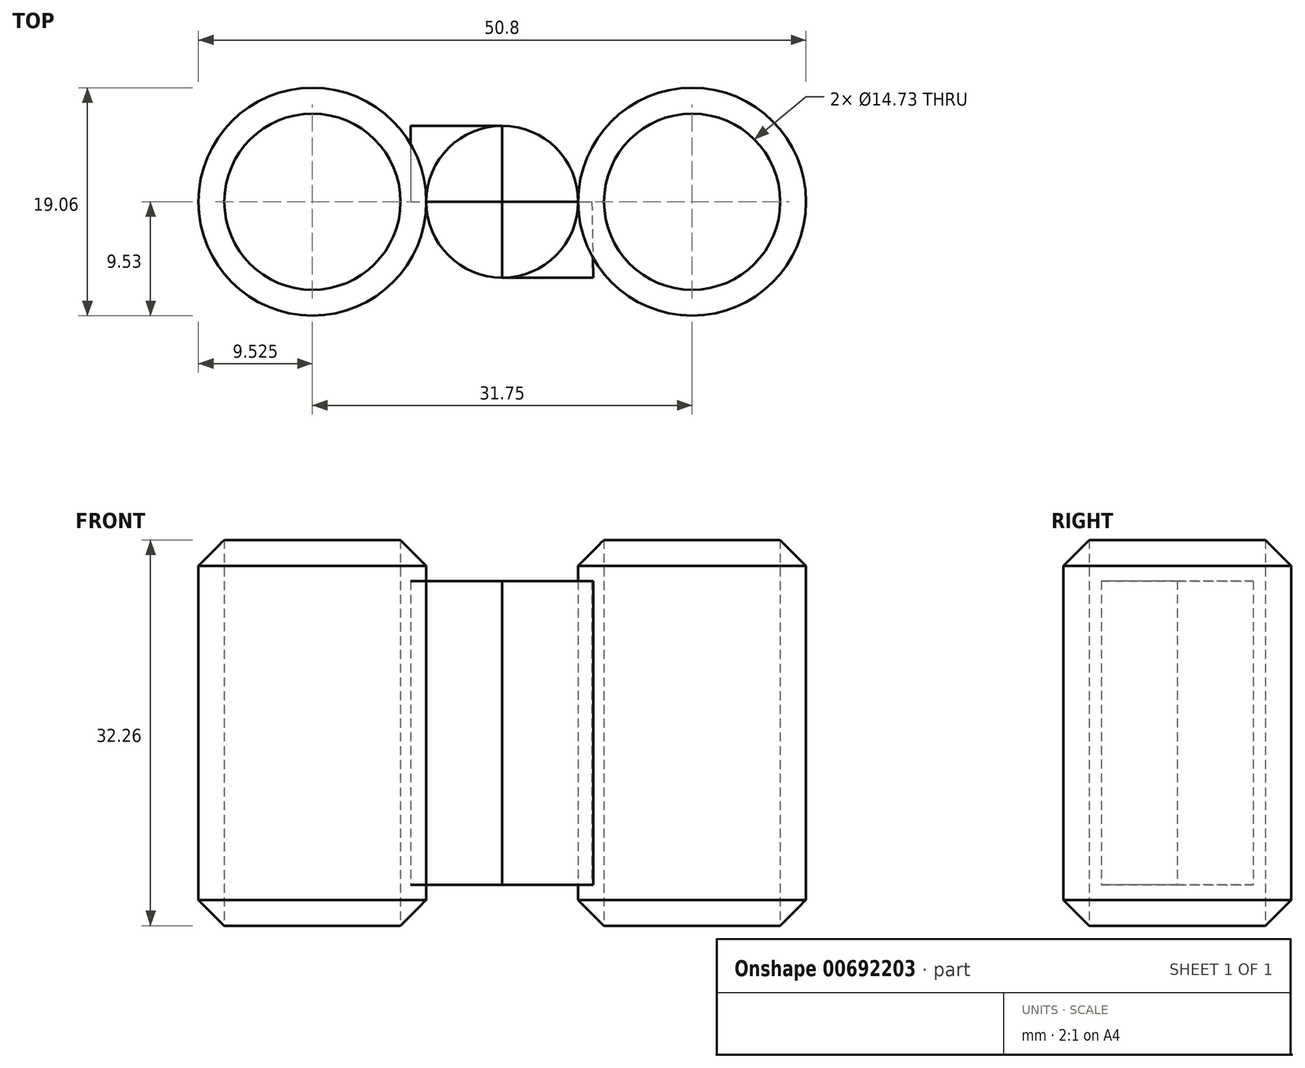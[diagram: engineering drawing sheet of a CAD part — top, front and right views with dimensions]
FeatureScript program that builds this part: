
annotation { "Feature Type Name" : "Feature", "Feature Type Description" : "" }
export const myFeature = defineFeature(function(context is Context, id is Id, definition is map)
    precondition{}
    {
        {
            var Q0;
            Q0=qCreatedBy(makeId("Top.planeOp"),FACE);
            var sketch = newSketch(context, id + "F0", { "sketchPlane" : qUnion([Q0])});
            skCircle(sketch, "E0", {"center": v(-15.88, 0) * mm, "radius": 7.37 * mm});
            skCircle(sketch, "E1.MirrorC", {"center": v(15.88, 0) * mm, "radius": 7.37 * mm});
            skCircle(sketch, "E2", {"center": v(-15.88, 0) * mm, "radius": 9.53 * mm});
            skCircle(sketch, "E3.MirrorC", {"center": v(15.88, 0) * mm, "radius": 9.53 * mm});
            skSolve(sketch);
        }
        {
            var Q0;
            Q0=qSketchRegion(id+"F0",true);
            extrude(context, id + "F1", {"entities" : qUnion([Q0]), "endBound" : BoundingType.SYMMETRIC, "depth" : 38.1 * mm, "offsetDistance" : 25.4 * mm});
        }
        {
            var Q0;
            Q0=qCreatedBy(makeId("Top.planeOp"),FACE);
            var sketch = newSketch(context, id + "F2", { "sketchPlane" : qUnion([Q0])});
            skCircle(sketch, "E4", {"center": v(0, 0) * mm, "radius": 6.35 * mm});
            skSolve(sketch);
        }
        {
            var Q0;
            Q0=qSketchRegion(id+"F2",true);
            extrude(context, id + "F3", {"entities" : qUnion([Q0]), "endBound" : BoundingType.SYMMETRIC, "depth" : 25.4 * mm, "offsetDistance" : 25.4 * mm});
        }
        {
            var Q0;
            Q0=qCreatedBy(makeId("Top.planeOp"),FACE);
            var sketch = newSketch(context, id + "F4", { "sketchPlane" : qUnion([Q0])});
            skLineSegment(sketch, "E5", {"start": v(0, 0) * mm, "end": v(0, 6.35) * mm});
            skLineSegment(sketch, "E6", {"start": v(0, 6.35) * mm, "end": v(-7.65, 6.35) * mm});
            skLineSegment(sketch, "E7", {"start": v(-7.65, 6.35) * mm, "end": v(7.6, 6.35) * mm});
            skPoint(sketch, "E7.endSnap0", {"position": v(-3.82, 6.35) * mm});
            skLineSegment(sketch, "E8", {"start": v(-7.65, 6.35) * mm, "end": v(-7.65, 0) * mm});
            skLineSegment(sketch, "E9", {"start": v(-7.65, 0) * mm, "end": v(7.5, 0) * mm});
            skLineSegment(sketch, "E10", {"start": v(7.5, 0) * mm, "end": v(7.6, 6.35) * mm});
            skLineSegment(sketch, "E11.MirrorCS", {"start": v(-7.65, -6.35) * mm, "end": v(7.6, -6.35) * mm});
            skLineSegment(sketch, "E12.MirrorCS", {"start": v(-7.65, -6.35) * mm, "end": v(-7.65, 0) * mm});
            skLineSegment(sketch, "E13.MirrorCS", {"start": v(7.5, 0) * mm, "end": v(7.6, -6.35) * mm});
            skLineSegment(sketch, "E14.MirrorCS", {"start": v(0, 0) * mm, "end": v(0, -6.35) * mm});
            skSolve(sketch);
        }
        {
            var Q0;
            {var subQ0=sQuery(id+"F4.wireOp",EDGE,"E5");Q0=makeQuery(id+"F4.imprint","IMPRINT",FACE,{"disambiguationData":[TD([[makeQuery(id+"F4.imprint","IMPRINT",EDGE,{"derivedFrom":subQ0}),1.0]])]});}
            var Q1;
            {var subQ2=sQuery(id+"F4.wireOp",EDGE,"E13.MirrorCS");Q1=makeQuery(id+"F4.imprint","IMPRINT",FACE,{"disambiguationData":[TD([[makeQuery(id+"F4.imprint","IMPRINT",EDGE,{"derivedFrom":subQ2}),-1.0]])]});}
            extrude(context, id + "F5", {"entities" : qUnion([Q0, Q1]), "endBound" : BoundingType.SYMMETRIC, "depth" : 25.4 * mm, "offsetDistance" : 25.4 * mm});
        }
        {
            var Q0;
            Q0=makeQuery(id+"F1.opExtrude","CAP_EDGE",EDGE,{"disambiguationData":[OSD([sQuery(id+"F0.wireOp",EDGE,"E3.MirrorC")])],"isStart":false});
            var Q1;
            Q1=makeQuery(id+"F1.opExtrude","CAP_EDGE",EDGE,{"disambiguationData":[OSD([sQuery(id+"F0.wireOp",EDGE,"E2")])],"isStart":false});
            var Q2;
            Q2=makeQuery(id+"F1.opExtrude","CAP_EDGE",EDGE,{"disambiguationData":[OSD([sQuery(id+"F0.wireOp",EDGE,"E3.MirrorC")])],"isStart":true});
            var Q3;
            Q3=makeQuery(id+"F1.opExtrude","CAP_EDGE",EDGE,{"disambiguationData":[OSD([sQuery(id+"F0.wireOp",EDGE,"E2")])],"isStart":true});
            chamfer(context, id + "F6", {"entities" : qUnion([Q0, Q1, Q2, Q3]), "width" : 5.08 * mm, "tangentPropagation" : true});
        }
    });
